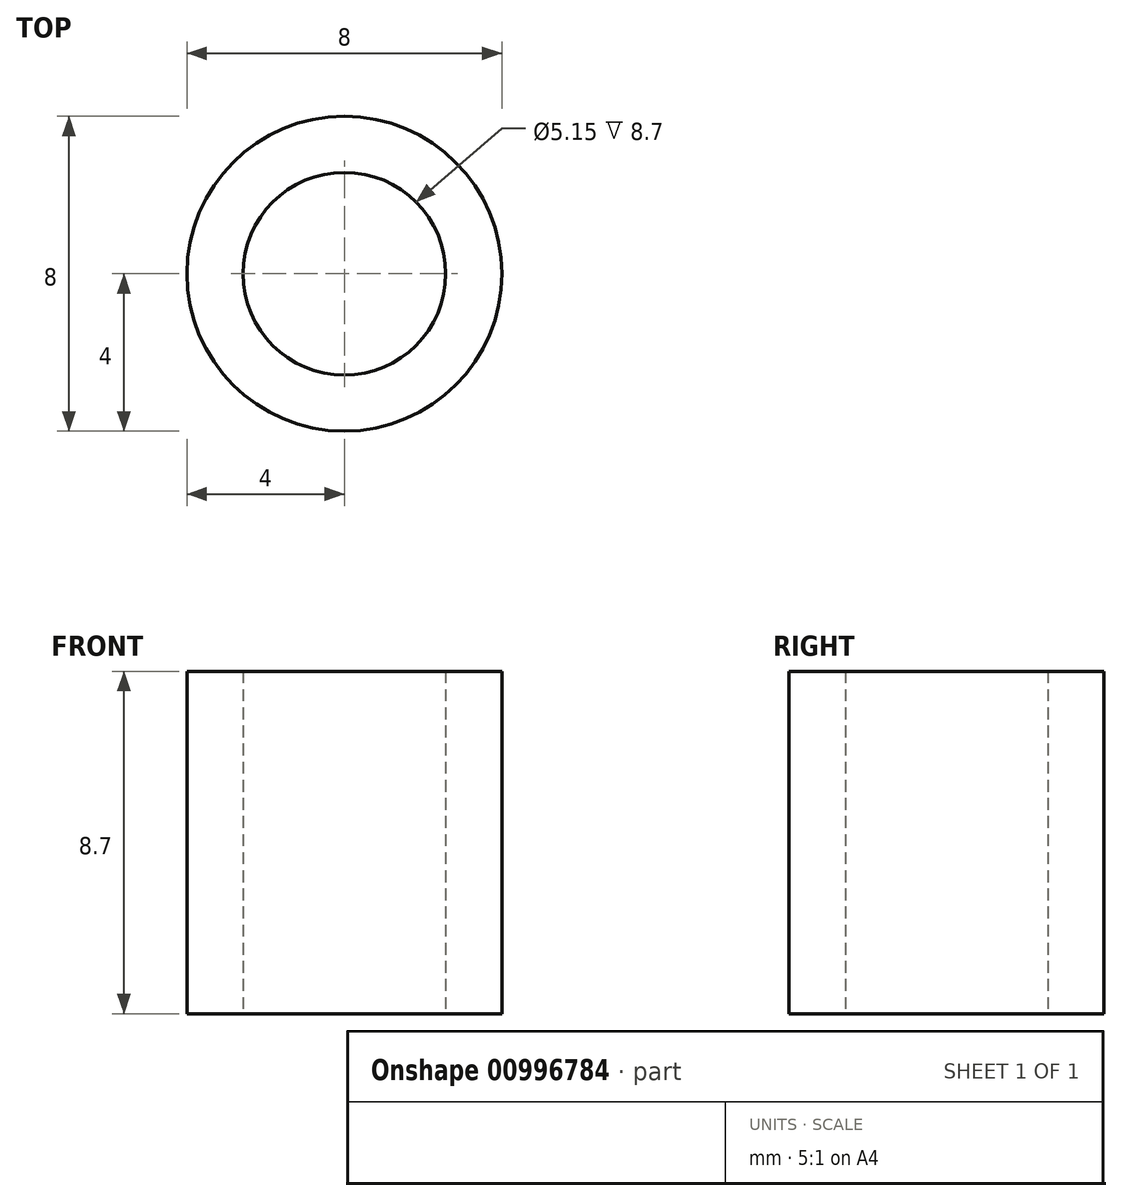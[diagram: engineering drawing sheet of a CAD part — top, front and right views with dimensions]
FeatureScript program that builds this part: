
annotation { "Feature Type Name" : "Feature", "Feature Type Description" : "" }
export const myFeature = defineFeature(function(context is Context, id is Id, definition is map)
    precondition{}
    {
        {
            var Q0;
            Q0=qCreatedBy(makeId("Top.planeOp"),FACE);
            var sketch = newSketch(context, id + "F0", { "sketchPlane" : qUnion([Q0])});
            skCircle(sketch, "E0", {"center": v(0, 0) * mm, "radius": 4 * mm});
            skCircle(sketch, "E1", {"center": v(0, 0) * mm, "radius": 2.58 * mm});
            skSolve(sketch);
        }
        {
            var Q0;
            Q0 = qSketchRegion(id + "F0", true);
            extrude(context, id + "F1", {"entities" : qUnion([Q0]), "depth" : 8.7 * mm, "offsetDistance" : 25 * mm});
        }
    });
